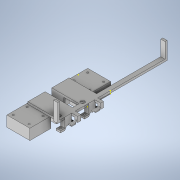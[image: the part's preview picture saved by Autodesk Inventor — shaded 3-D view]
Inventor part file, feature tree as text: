
AUTODESK INVENTOR PART (.ipt)
format: ipt  version: 2020.2 (Build 242310000, 310)  size: 1,021,440 bytes
history: native  units: mm
features: sketch x43, extrude x38, projected_geometry x19, hole x5
ambient origin geometry x8: Origin, YZ Plane, XZ Plane, XY Plane, X Axis, Y Axis, Z Axis, Center Point
bodies: Solid1 (feature_tree)
feature tree (105):
  sketch  "Sketch1"  dims[d0=8.0mm d1=98.298mm]
  extrude  "Extrusion1"  Depth=98.298mm
  extrude  "Extrusion2"  Depth=4.0mm
  extrude  "Extrusion3"  Depth=4.0mm TaperAngle=0.0deg
  extrude  "Extrusion4"  Depth=34.0mm
  extrude  "Extrusion5"  Depth=12.7mm
  extrude  "Extrusion6"  Depth=25.0mm
  hole  "Hole1"  [1 undecoded]
  extrude  "Extrusion11"  TaperAngle=60.0deg  [1 undecoded]
  extrude  "Extrusion12"  TaperAngle=120.0deg  [1 undecoded]
  sketch  "Sketch16"  dims[d19=6.4262mm d20=120.0deg]
  extrude  "Extrusion13"  Depth=6.4262mm
  extrude  "Extrusion14"  Depth=6.4262mm
  sketch  "Sketch17"  dims[d21=120.0deg d22=6.4262mm]
  extrude  "Extrusion15"  Depth=25.4mm TaperAngle=0.0deg
  extrude  "Extrusion18"  Depth=12.8016mm
  extrude  "Extrusion19"  Depth=12.8016mm
  extrude  "Extrusion20"  Depth=10.0mm
  hole  "Hole2"  [1 undecoded]
  extrude  "Extrusion21"  Depth=2.0mm
  extrude  "Extrusion22"  Depth=2.0mm
  sketch  "Sketch27"  dims[d45=12.8016mm d46=2.0mm]
  extrude  "Extrusion23"  Depth=25.4mm
  extrude  "Extrusion24"  Depth=32.48mm
  extrude  "Extrusion25"  TaperAngle=90.0deg  [1 undecoded]
  sketch  "Sketch29"  dims[d79=51.53mm d80=32.48mm]
  extrude  "Extrusion26"  Depth=2.0mm
  extrude  "Extrusion27"  Depth=21.0mm
  extrude  "Extrusion28"  Depth=36.0mm TaperAngle=0.0deg
  extrude  "Extrusion29"  Depth=8.0mm
  extrude  "Extrusion30"  Depth=17.5mm
  extrude  "Extrusion32"  Depth=35.0mm
  extrude  "Extrusion38"  Depth=5.0mm
  extrude  "Extrusion39"  TaperAngle=90.0deg  [1 undecoded]
  extrude  "Extrusion40"  Depth=5.0mm
  hole  "Hole4"  [1 undecoded]
  extrude  "Extrusion43"  Depth=1.5mm
  extrude  "Extrusion44"  TaperAngle=0.0deg  [1 undecoded]
  extrude  "Extrusion45"  Depth=28.8036mm
  extrude  "Extrusion46"  Depth=25.4mm
  extrude  "Extrusion47"  TaperAngle=120.0deg  [1 undecoded]
  extrude  "Extrusion48"  Depth=6.4262mm
  extrude  "Extrusion49"  Depth=25.4mm TaperAngle=0.0deg
  extrude  "Extrusion50"  Depth=17.78mm
  sketch  "Sketch56"  dims[d135=3.2131mm d136=6.4262mm]
  sketch  "Sketch58"  dims[d137=120.0deg d138=25.4mm d139=0.0mm]
  extrude  "Extrusion53"  TaperAngle=0.0deg  [1 undecoded]
  hole  "Hole5"  [1 undecoded]
  sketch  "Sketch62"  dims[d144=25.4mm d145=0.0mm d146=10.0mm]
  extrude  "Extrusion54"  Depth=12.7mm
  hole  "Hole6"  [1 undecoded]
  sketch  "Sketch2"  dims[d2=8.0mm d3=4.0mm]
  sketch  "Sketch3"  dims[d4=4.0mm d5=4.0mm d6=0.0mm]
  sketch  "Sketch4"  dims[d7=34.0mm d8=0.0mm d9=19.558mm]
  sketch  "Sketch5"  dims[d10=16.1125mm d11=12.7mm]
  sketch  "Sketch6"  dims[d12=25.0mm d13=0.0mm d14=7.2009mm]
  sketch  "Sketch14"  dims[d15=6.4135mm d16=12.827mm]
  projected_geometry  "Projected Loop2"
  sketch  "Sketch15"  dims[d17=6.4262mm d18=60.0deg]
  projected_geometry  "Projected Loop3"
  sketch  "Sketch18"  dims[d23=120.0deg d24=6.4262mm]
  sketch  "Sketch21"  dims[d25=120.0deg d26=25.4mm d27=0.0mm]
  sketch  "Sketch22"  dims[d28=6.0mm d29=12.8016mm]
  sketch  "Sketch23"  dims[d30=5.9944mm d31=12.8016mm]
  sketch  "Sketch24"  dims[d32=25.4mm d33=0.0mm d34=10.0mm]
  sketch  "Sketch25"  dims[d35=90.0deg d36=20.0mm]
  projected_geometry  "Projected Loop5"
  sketch  "Sketch26"  dims[d37=3.4mm d38=19.05mm d39=6.2992mm d40=6.35mm d41=90.0deg d42=5.0mm d43=0.0mm d44=2.0mm]
  sketch  "Sketch28"  dims[d47=25.4mm d48=0.0mm d78=16.24mm]
  sketch  "Sketch30"  dims[d81=90.0deg d82=90.0deg]
  sketch  "Sketch32"  dims[d83=4.0mm d84=0.0mm d87=2.0mm]
  projected_geometry  "Projected Loop6"
  sketch  "Sketch33"  dims[d88=2.0mm d89=21.0mm]
  projected_geometry  "Projected Loop7"
  sketch  "Sketch35"  dims[d90=2.0mm d91=36.0mm d92=0.0mm]
  projected_geometry  "Projected Loop8"
  sketch  "Sketch42"  dims[d93=17.78mm d94=8.0mm]
  sketch  "Sketch43"  dims[d95=180.0deg d96=17.5mm]
  projected_geometry  "Projected Loop9"
  projected_geometry  "Projected Loop10"
  projected_geometry  "Projected Loop11"
  projected_geometry  "Projected Loop12"
  sketch  "Sketch44"  dims[d97=90.0deg d98=35.0mm]
  sketch  "Sketch45"  dims[d99=3.5mm d100=5.0mm]
  sketch  "Sketch48"  dims[d101=7.0mm d102=90.0deg]
  sketch  "Sketch49"  dims[d103=5.0mm d104=3.4mm]
  projected_geometry  "Projected Loop13"
  projected_geometry  "Projected Loop14"
  sketch  "Sketch50"  dims[d105=3.4mm d106=25.4mm d107=0.0mm]
  projected_geometry  "Projected Loop15"
  sketch  "Sketch51"  dims[d108=6.4262mm d109=0.0mm d110=1.5mm]
  sketch  "Sketch52"  dims[d111=1.5mm d112=0.0mm d113=0.0mm]
  sketch  "Sketch53"  dims[d128=44.8mm d129=28.8036mm]
  projected_geometry  "Projected Loop16"
  projected_geometry  "Projected Loop17"
  projected_geometry  "Projected Loop18"
  projected_geometry  "Projected Loop19"
  sketch  "Sketch54"  dims[d130=25.4mm d131=0.0mm d132=3.2131mm]
  sketch  "Sketch55"  dims[d133=6.4262mm d134=120.0deg]
  projected_geometry  "Projected Loop20"
  projected_geometry  "Projected Loop21"
  sketch  "Sketch60"  dims[d140=8.001mm d141=17.78mm]
  sketch  "Sketch61"  dims[d142=8.001mm d143=0.0mm]
  sketch  "Sketch63"  dims[d147=20.0mm]
  sketch  "Sketch64"  dims[d148=3.4mm d149=19.05mm d150=6.2992mm d151=6.35mm d152=90.0deg d153=5.0mm d154=0.0mm d155=16.2433mm d156=32.4866mm d157=51.5366mm d158=4.0mm d159=0.0mm d160=21.0mm d161=2.0mm d162=2.0mm d163=2.0mm d164=2.0mm d165=36.0mm d166=0.0mm d167=7.0mm d168=5.0mm d169=5.0mm d170=17.5mm d171=35.0mm d172=3.4mm d173=3.4mm d174=5.0mm d175=0.0mm d176=5.0mm d177=0.0mm d178=1.5mm d179=1.5mm d180=25.4mm d181=0.0mm d182=19.05mm d183=10.0mm d184=5.08mm d185=4.0mm d186=0.0mm d187=10.0mm d188=0.0mm d189=2.0mm d190=3.0mm d191=25.4mm d192=0.0mm d194=30.0mm d195=0.0mm d196=102.489mm d197=0.0mm d201=11.43mm d202=0.0mm d239=25.4mm d240=0.0mm d241=1.5mm d242=0.0mm d243=39.0mm d244=35.0mm d245=39.0mm d246=35.0mm d247=3.0mm d248=0.0mm d249=5.0mm d250=5.0mm d251=29.7mm d252=26.05mm d253=4.0mm d254=4.0mm d255=29.7mm d256=26.05mm d257=3.4mm d258=19.05mm d259=6.2992mm d260=6.35mm d261=90.0deg d262=25.4mm d263=20.594885mm d271=4.0mm d272=28.4mm d273=0.0mm d274=25.4mm d275=0.0mm d276=3.429mm d277=180.0deg d278=30.0mm d279=0.0mm d280=6.35mm d281=25.4mm d282=0.0mm d283=5.08mm d284=25.4mm d285=0.0mm d286=2.0mm d287=0.0mm d288=12.7mm d289=0.0mm d290=2.0mm d291=42.9956mm d292=37.0012mm d293=37.0012mm d294=2.0mm d295=2.0mm d296=20.0mm d297=0.0mm d298=15.0086mm d299=2.0mm d312=7.62mm d313=1.9812mm d314=12.7mm d315=0.0mm d316=5.0mm d317=0.0mm d318=3.4036mm d319=19.05mm d320=7.62mm d321=1.27mm d322=90.0deg d323=25.4mm d324=20.594885mm d325=7.62mm d326=12.7mm d327=0.0mm d328=5.0mm d329=3.4036mm d330=19.05mm d331=7.62mm d332=1.27mm d333=90.0deg d334=25.4mm d335=20.594885mm d214=12.7mm d215=0.872665mm d216=12.7mm d217=0.872665mm d228=12.7mm d229=0.872665mm d230=12.7mm d231=0.872665mm]
note: 12 required parameter values undecoded (feature->parameter linkage not recoverable at this tier; creation-order binding heuristic only, values carry confidence <= 0.55)
